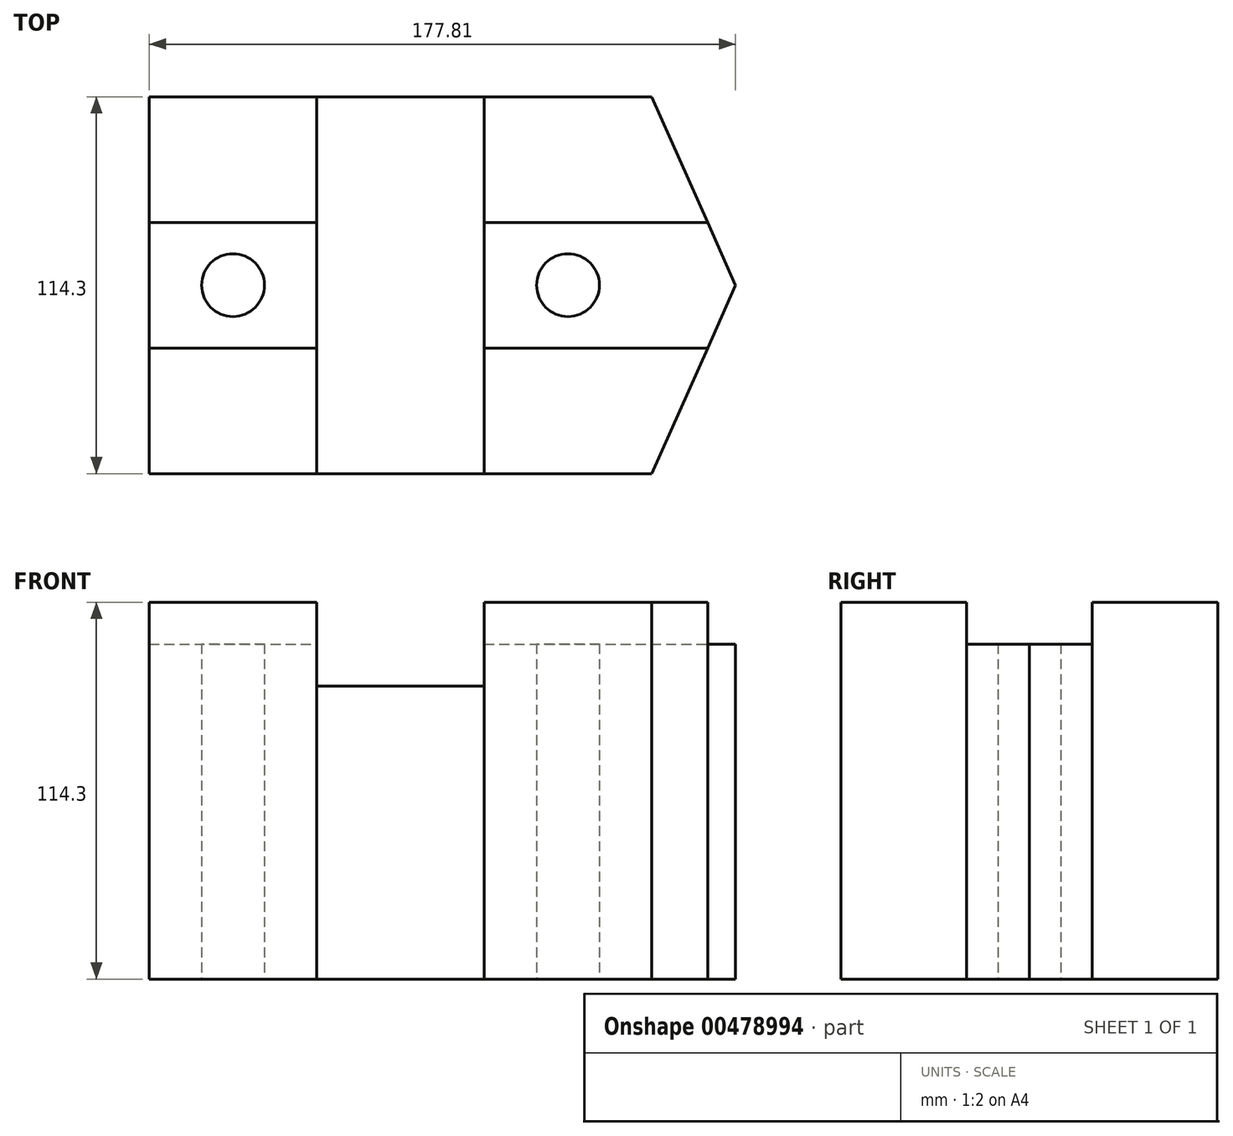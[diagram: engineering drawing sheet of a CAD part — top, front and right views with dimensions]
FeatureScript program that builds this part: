
annotation { "Feature Type Name" : "Feature", "Feature Type Description" : "" }
export const myFeature = defineFeature(function(context is Context, id is Id, definition is map)
    precondition{}
    {
        {
            var Q0;
            Q0=qCreatedBy(makeId("Top.planeOp"),FACE);
            var sketch = newSketch(context, id + "F0", { "sketchPlane" : qUnion([Q0])});
            skLineSegment(sketch, "E0", {"start": v(152.4, 0) * mm, "end": v(0, 0) * mm});
            skLineSegment(sketch, "E1", {"start": v(0, 0) * mm, "end": v(0, 38.1) * mm});
            skLineSegment(sketch, "E2", {"start": v(0, 38.1) * mm, "end": v(0, 76.2) * mm});
            skLineSegment(sketch, "E3", {"start": v(0, 76.2) * mm, "end": v(0, 114.3) * mm});
            skLineSegment(sketch, "E4", {"start": v(0, 114.3) * mm, "end": v(50.8, 114.3) * mm});
            skLineSegment(sketch, "E5", {"start": v(50.8, 114.3) * mm, "end": v(101.6, 114.3) * mm});
            skLineSegment(sketch, "E6", {"start": v(101.6, 114.3) * mm, "end": v(152.4, 114.3) * mm});
            skLineSegment(sketch, "E7", {"start": v(50.8, 114.3) * mm, "end": v(50.8, 0) * mm});
            skLineSegment(sketch, "E8", {"start": v(101.6, 114.3) * mm, "end": v(101.6, 0) * mm});
            skLineSegment(sketch, "E9", {"start": v(177.8, 57.15) * mm, "end": v(152.4, 114.3) * mm});
            skLineSegment(sketch, "E10", {"start": v(177.8, 57.15) * mm, "end": v(152.4, 0) * mm});
            skLineSegment(sketch, "E11", {"start": v(0, 76.2) * mm, "end": v(50.8, 76.2) * mm});
            skLineSegment(sketch, "E12", {"start": v(0, 38.1) * mm, "end": v(50.8, 38.1) * mm});
            skLineSegment(sketch, "E13", {"start": v(101.6, 38.1) * mm, "end": v(152.4, 38.1) * mm});
            skLineSegment(sketch, "E14", {"start": v(101.6, 76.2) * mm, "end": v(152.4, 76.2) * mm});
            skLineSegment(sketch, "E15", {"start": v(152.4, 76.2) * mm, "end": v(169.34, 76.2) * mm});
            skLineSegment(sketch, "E16", {"start": v(152.4, 38.1) * mm, "end": v(169.34, 38.1) * mm});
            skPoint(sketch, "E17.endSnap0", {"position": v(0, 57.15) * mm});
            skCircle(sketch, "E18", {"center": v(25.4, 57.15) * mm, "radius": 9.53 * mm});
            skCircle(sketch, "E19", {"center": v(127, 57.15) * mm, "radius": 9.53 * mm});
            skSolve(sketch);
        }
        {
            var Q0;
            {var subQ0=sQuery(id+"F0.wireOp",EDGE,"E1");Q0=makeQuery(id+"F0.imprint","IMPRINT",FACE,{"disambiguationData":[TD([[makeQuery(id+"F0.imprint","IMPRINT",EDGE,{"derivedFrom":subQ0}),-1.0]])]});}
            var Q1;
            {var subQ0=sQuery(id+"F0.wireOp",EDGE,"E13");Q1=makeQuery(id+"F0.imprint","IMPRINT",FACE,{"disambiguationData":[TD([[makeQuery(id+"F0.imprint","IMPRINT",EDGE,{"derivedFrom":subQ0}),-1.0]])]});}
            var Q2;
            {var subQ1=sQuery(id+"F0.wireOp",EDGE,"E6");Q2=makeQuery(id+"F0.imprint","IMPRINT",FACE,{"disambiguationData":[TD([[makeQuery(id+"F0.imprint","IMPRINT",EDGE,{"derivedFrom":subQ1}),-1.0]])]});}
            var Q3;
            Q3=makeQuery(id+"F0.imprint","IMPRINT",FACE,{"disambiguationData":[TD([[makeQuery(id+"F0.imprint","IMPRINT",EDGE,{"derivedFrom":sQuery(id+"F0.wireOp",EDGE,"E3")}),-1.0]])]});
            extrude(context, id + "F1", {"entities" : qUnion([Q0, Q1, Q2, Q3]), "depth" : 114.3 * mm});
        }
        {
            var Q0;
            {var subQ3=sQuery(id+"F0.wireOp",EDGE,"E5");Q0=makeQuery(id+"F0.imprint","IMPRINT",FACE,{"disambiguationData":[TD([[makeQuery(id+"F0.imprint","IMPRINT",EDGE,{"derivedFrom":subQ3}),-1.0]])]});}
            extrude(context, id + "F2", {"entities" : qUnion([Q0]), "depth" : 88.9 * mm});
        }
        {
            var Q0;
            Q0=makeQuery(id+"F0.imprint","IMPRINT",FACE,{"disambiguationData":[TD([[makeQuery(id+"F0.imprint","IMPRINT",EDGE,{"derivedFrom":sQuery(id+"F0.wireOp",EDGE,"E2")}),-1.0]])]});
            var Q1;
            {var subQ0=sQuery(id+"F0.wireOp",EDGE,"E13");Q1=makeQuery(id+"F0.imprint","IMPRINT",FACE,{"disambiguationData":[TD([[makeQuery(id+"F0.imprint","IMPRINT",EDGE,{"derivedFrom":subQ0}),1.0]])]});}
            extrude(context, id + "F3", {"entities" : qUnion([Q0, Q1]), "depth" : 101.6 * mm});
        }
    });
